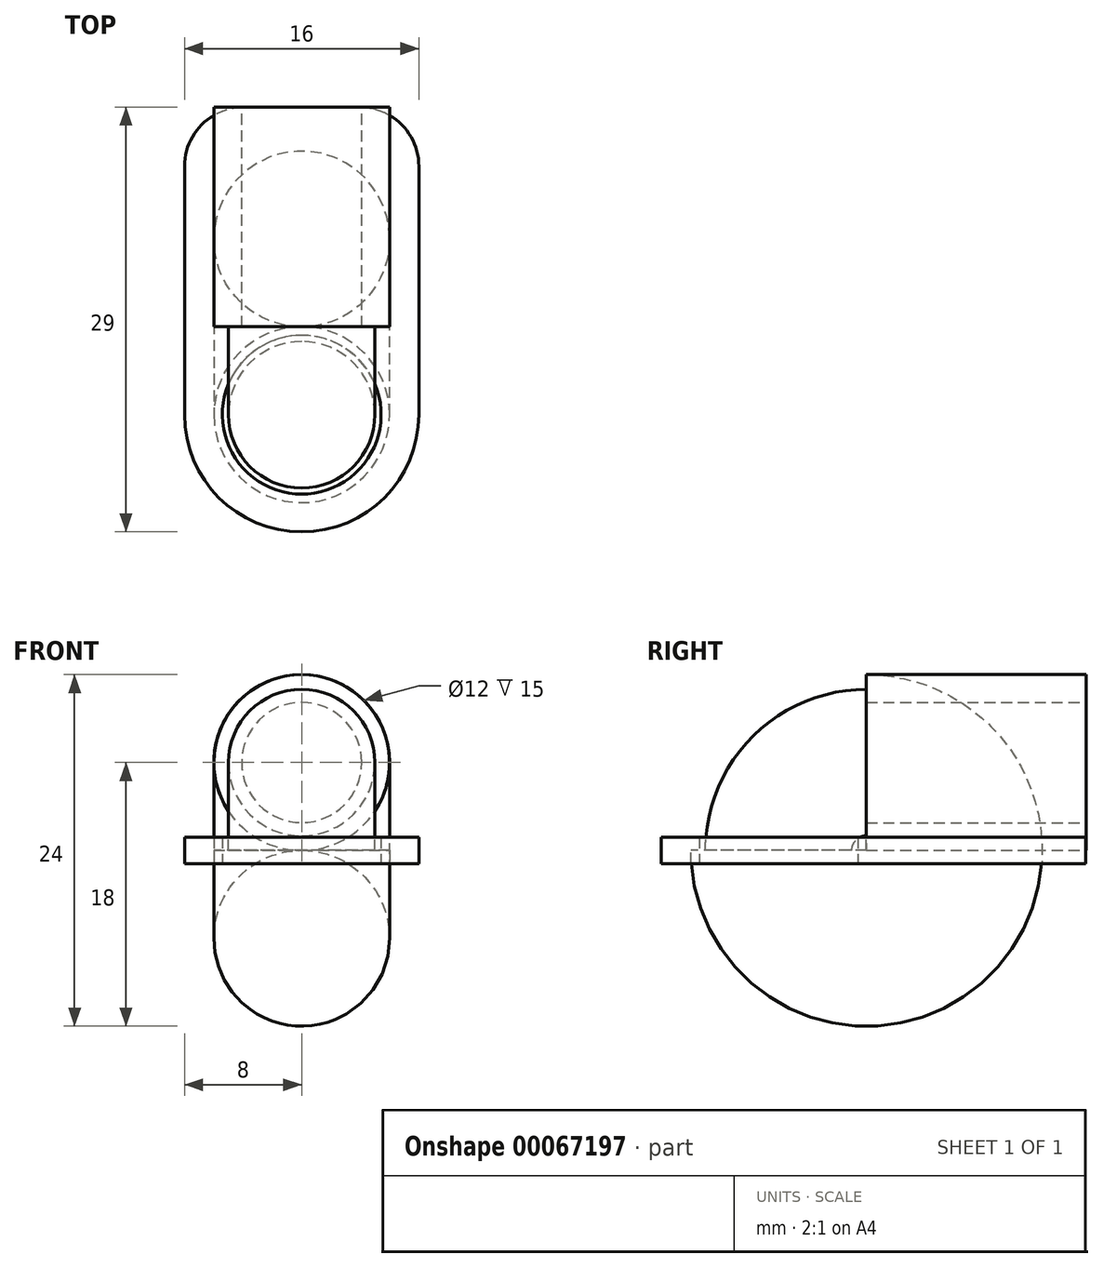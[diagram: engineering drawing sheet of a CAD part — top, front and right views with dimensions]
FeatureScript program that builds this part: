
annotation { "Feature Type Name" : "Feature", "Feature Type Description" : "" }
export const myFeature = defineFeature(function(context is Context, id is Id, definition is map)
    precondition{}
    {
        {
            var Q0;
            Q0=qCreatedBy(makeId("Front.planeOp"),FACE);
            var sketch = newSketch(context, id + "F0", { "sketchPlane" : qUnion([Q0])});
            skCircle(sketch, "E0", {"center": v(0, 0) * mm, "radius": 4.1 * mm});
            skCircle(sketch, "E1", {"center": v(0, 0) * mm, "radius": 6 * mm});
            skSolve(sketch);
        }
        {
            var Q0;
            Q0 = qSketchRegion(id + "F0", true);
            extrude(context, id + "F1", {"entities" : qUnion([Q0]), "depth" : 15 * mm});
        }
        {
            var Q0;
            Q0=makeQuery(id+"F1.opExtrude","CAP_FACE",FACE,{"disambiguationData":[OSD([sQuery(id+"F0.wireOp",EDGE,"E0"),sQuery(id+"F0.wireOp",EDGE,"E1")])],"isStart":false});
            var sketch = newSketch(context, id + "F2", { "sketchPlane" : qUnion([Q0])});
            skCircle(sketch, "E2", {"center": v(0, 0) * mm, "radius": 5 * mm});
            skLineSegment(sketch, "E3", {"start": v(0, 10.28) * mm, "end": v(0, -9.85) * mm, "construction": true});
            skLineSegment(sketch, "E4", {"start": v(8.67, -6) * mm, "end": v(-9.01, -6) * mm, "construction": true});
            skCircle(sketch, "E5", {"center": v(0, 0) * mm, "radius": 6 * mm});
            skSolve(sketch);
        }
        {
            var Q0;
            Q0=makeQuery(id+"F2.imprint","IMPRINT",FACE,{"disambiguationData":[TD([[makeQuery(id+"F2.imprint","IMPRINT",EDGE,{"derivedFrom":sQuery(id+"F2.wireOp",EDGE,"E2")}),-1.0]])]});
            var Q1;
            Q1=sQuery(id+"F2.wireOp",EDGE,"E4");
            revolve(context, id + "F3", {"operationType" : NewBodyOperationType.ADD, "entities" : qUnion([Q0]), "axis" : qUnion([Q1]), "revolveType" : RevolveType.ONE_DIRECTION, "oppositeDirection" : true, "angle" : 90 * degree});
        }
        {
            var Q0;
            Q0=makeQuery(id+"F3.opRevolve","CAP_FACE",FACE,{"disambiguationData":[OSD([sQuery(id+"F2.wireOp",EDGE,"E2"),sQuery(id+"F2.wireOp",EDGE,"E5")])],"isStart":false});
            var sketch = newSketch(context, id + "F4", { "sketchPlane" : qUnion([Q0])});
            skLineSegment(sketch, "E6", {"start": v(-4, 0.03) * mm, "end": v(4, 0.03) * mm});
            skLineSegment(sketch, "E7", {"start": v(8, 4.03) * mm, "end": v(8, 21) * mm});
            skArc(sketch, "E8", {"start": v(8, 21) * mm, "mid": v(0, 29) * mm, "end": v(-8, 21) * mm});
            skLineSegment(sketch, "E9", {"start": v(-8, 21) * mm, "end": v(-8, 4.03) * mm});
            skPoint(sketch, "E10.visualSharp", {"position": v(-8, 0.03) * mm});
            skArc(sketch, "E10.filletArc", {"start": v(-8, 4.03) * mm, "mid": v(-6.83, 1.2) * mm, "end": v(-4, 0.03) * mm});
            skPoint(sketch, "E11.visualSharp", {"position": v(8, 0.03) * mm});
            skArc(sketch, "E11.filletArc", {"start": v(4, 0.03) * mm, "mid": v(6.83, 1.2) * mm, "end": v(8, 4.03) * mm});
            skPoint(sketch, "E12.0", {"position": v(0, 0) * mm});
            skCircle(sketch, "E13", {"center": v(0, 21) * mm, "radius": 5.42 * mm});
            skSolve(sketch);
        }
        {
            var Q0;
            Q0=makeQuery(id+"F4.imprint","IMPRINT",FACE,{"disambiguationData":[TD([[makeQuery(id+"F4.imprint","IMPRINT",EDGE,{"derivedFrom":sQuery(id+"F4.wireOp",EDGE,"E6")}),1.0]])]});
            var Q1;
            Q1=makeQuery(id+"F4.imprint","IMPRINT",FACE,{"disambiguationData":[TD([[makeQuery(id+"F4.imprint","IMPRINT",EDGE,{"derivedFrom":sQuery(id+"F4.wireOp",EDGE,"E13")}),-1.0]])]});
            extrude(context, id + "F5", {"entities" : qUnion([Q0, Q1]), "oppositeDirection" : true, "depth" : 1.8 * mm, "symmetric" : true});
        }
    });
